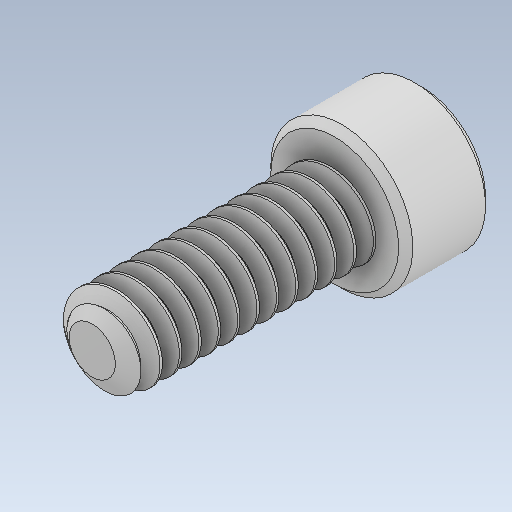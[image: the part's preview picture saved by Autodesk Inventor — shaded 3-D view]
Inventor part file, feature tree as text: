
AUTODESK INVENTOR PART (.ipt)
format: ipt  version: 2020 (Build 240168000, 168)  size: 583,168 bytes
history: native  units: in
note: dims shown in document units (in); Inventor stores cm internally (conversion verified against a paired STEP export)
features: chamfer x1
ambient origin geometry x8: Origin, YZ Plane, XZ Plane, XY Plane, X Axis, Y Axis, Z Axis, Center Point
bodies: Solid1 (feature_tree)
feature tree (1):
  chamfer  "Chamfer1"  [1 undecoded]
note: 1 required parameter value undecoded (feature->parameter linkage not recoverable at this tier; creation-order binding heuristic only, values carry confidence <= 0.55)
